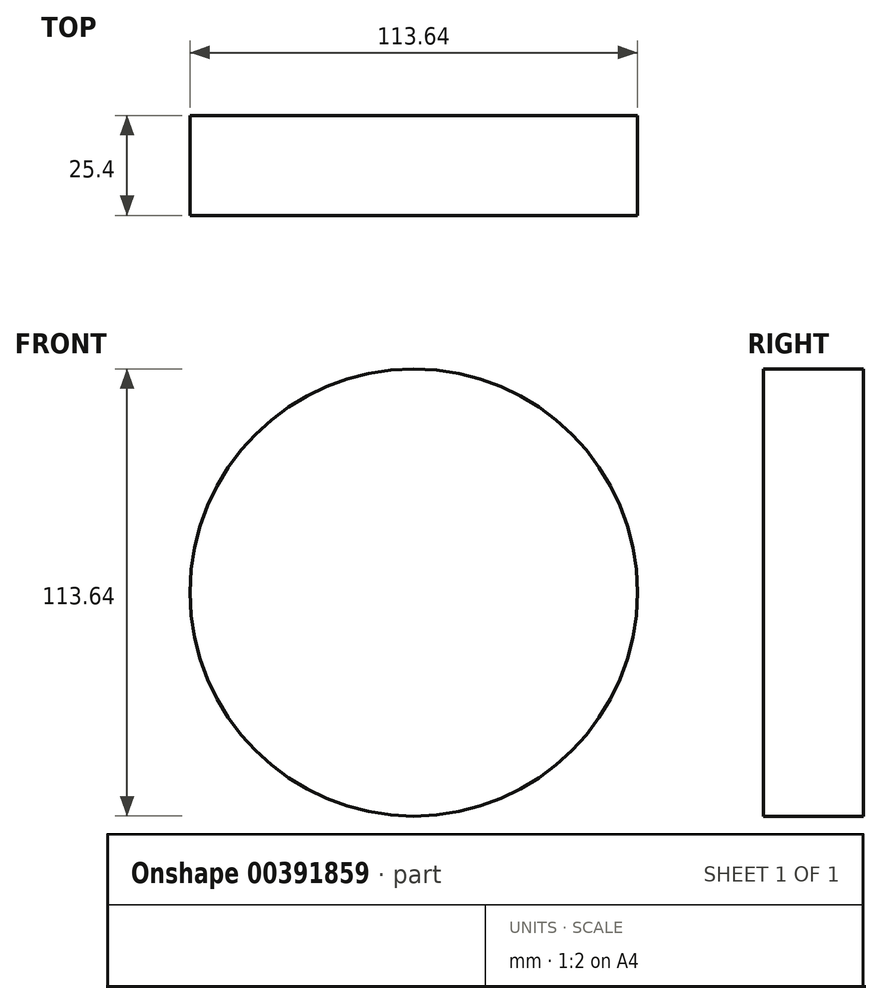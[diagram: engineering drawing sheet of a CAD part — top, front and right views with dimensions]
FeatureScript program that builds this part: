
annotation { "Feature Type Name" : "Feature", "Feature Type Description" : "" }
export const myFeature = defineFeature(function(context is Context, id is Id, definition is map)
    precondition{}
    {
        {
            var Q0;
            Q0=qCreatedBy(makeId("Front.planeOp"),FACE);
            var sketch = newSketch(context, id + "F0", { "sketchPlane" : qUnion([Q0])});
            skCircle(sketch, "E0", {"center": v(0, 0) * mm, "radius": 56.82 * mm});
            skSolve(sketch);
        }
        {
            var Q0;
            Q0=makeQuery(id+"F0.imprint","IMPRINT",FACE,{"disambiguationData":[TD([[makeQuery(id+"F0.imprint","IMPRINT",EDGE,{"derivedFrom":sQuery(id+"F0.wireOp",EDGE,"E0")}),1.0]])]});
            extrude(context, id + "F1", {"entities" : qUnion([Q0]), "depth" : 25.4 * mm});
        }
    });
